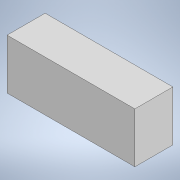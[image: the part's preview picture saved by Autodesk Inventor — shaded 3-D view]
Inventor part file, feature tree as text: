
AUTODESK INVENTOR PART (.ipt)
format: ipt  version: 2022.1 (Build 261234000, 234)  size: 88,064 bytes
history: native  units: mm
features: extrude x1, sketch x1
ambient origin geometry x8: Origin, YZ Plane, XZ Plane, XY Plane, X Axis, Y Axis, Z Axis, Center Point
bodies: Solid1 (feature_tree)
feature tree (2):
  extrude  "Extrusion1"  Depth=26.4mm
  sketch  "Sketch1"  dims[d0=67.2mm d1=26.4mm d2=20.0mm d3=0.0mm]
